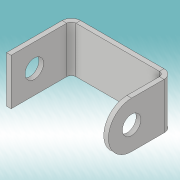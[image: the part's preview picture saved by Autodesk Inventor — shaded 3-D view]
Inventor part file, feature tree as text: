
AUTODESK INVENTOR PART (.ipt)
format: ipt  version: 2019 (Build 230136000, 136)  size: 159,744 bytes
history: native  units: in
note: dims shown in document units (in); Inventor stores cm internally (conversion verified against a paired STEP export)
features: sketch x5, sheet_metal_op x3, other x3, extrude x2
ambient origin geometry x8: Origin, YZ Plane, XZ Plane, XY Plane, X Axis, Y Axis, Z Axis, Center Point
bodies: Solid1 (feature_tree)
feature tree (13):
  extrude  "Extrusion1"  Depth=0.7874in
  sheet_metal_op  "Flange1"
  extrude  "Extrusion2"  Depth=0.0787in
  sketch  "Sketch1"  dims[d0=1.7323in d1=0.7874in]
  sketch  "Sketch2"  dims[d2=0.0787in d3=0.0in d4=0.0787in]
  other  "Plate1"
  sheet_metal_op  "Bend1"
  sheet_metal_op  "Corner1"
  sketch  "Sketch3"  dims[d5=0.0787in]
  sketch  "Sketch4"  dims[d6=0.0394in]
  sketch  "Sketch5"  dims[d7=0.1575in d8=0.0787in d9=1.1024in d10=90.0deg d11=0.0787in d12=0.315in d13=0.0787in d14=0.0787in d15=0.3937in d16=0.315in d17=0.0787in d18=0.0in d19=0.0787in d20=0.0in d21=0.3543in d22=0.7087in d23=0.3937in d24=0.0039in d25=0.0in]
  other  "Cut1"
  other  "Cut2"
